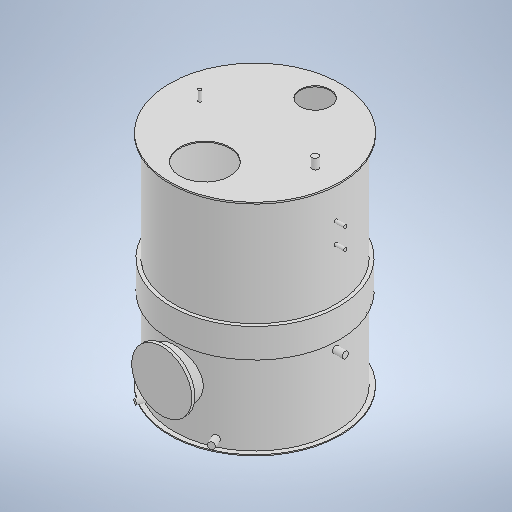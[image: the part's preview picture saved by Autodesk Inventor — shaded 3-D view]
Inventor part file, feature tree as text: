
AUTODESK INVENTOR PART (.ipt)
format: ipt  version: 2025 (Build 290162010, 162A)  size: 396,288 bytes
history: native  units: mm
features: sketch x9, extrude x8, plane x2, revolve x1, shell x1, projected_geometry x1
ambient origin geometry x8: Origin, YZ Plane, XZ Plane, XY Plane, X Axis, Y Axis, Z Axis, Center Point
bodies: Body1 (feature_tree)
feature tree (22):
  revolve  "Revolution1"  [1 undecoded]
  extrude  "Extrusion2"  Depth=1700.0mm
  extrude  "Extrusion8"  Depth=16.0mm
  plane  "Work Plane1"
  plane  "Work Plane2"
  extrude  "Extrusion3"  Depth=1680.0mm
  extrude  "Extrusion4"  Depth=500.0mm
  extrude  "Extrusion5"  Depth=900.0mm TaperAngle=0.0deg
  extrude  "Extrusion6"  Depth=30.0mm TaperAngle=0.0deg
  extrude  "Extrusion7"  Depth=1820.0mm
  extrude  "Extrusion9"  Depth=10.0mm
  shell  "Shell1"  Thickness=65.0mm
  sketch  "Sketch3"  dims[d3=2190.0mm d4=10.0mm]
  sketch  "Sketch4"  dims[d6=1610.0mm d7=1700.0mm]
  sketch  "Sketch5"  dims[d8=16.0mm d9=290.0mm]
  projected_geometry  "Projected Loop2"
  sketch  "Sketch6"  dims[d10=810.0mm d11=1680.0mm]
  sketch  "Sketch7"  dims[d12=90.0deg d13=500.0mm]
  sketch  "Sketch8"  dims[d14=500.0mm d15=900.0mm d16=0.0mm]
  sketch  "Sketch9"  dims[d17=600.0mm d18=30.0mm d19=0.0mm]
  sketch  "Sketch10"  dims[d20=710.0mm d21=1820.0mm]
  sketch  "Sketch11"  dims[d22=1620.0mm d23=32.0mm d24=65.0mm d25=900.0mm d26=0.0mm d27=300.0mm d28=710.0mm d29=1360.0mm d30=65.0mm d31=32.0mm d32=900.0mm d33=0.0mm d34=4.363323mm d35=65.0mm d36=85.0mm d37=900.0mm d38=0.0mm d39=-4.363323mm d40=50.0mm d41=85.0mm d42=900.0mm d43=0.0mm d44=500.0mm d45=300.0mm d46=100.0mm d47=10.0mm d48=0.0mm d49=65.0mm d50=32.0mm d51=250.0mm d52=300.0mm d53=100.0mm d54=0.0mm d55=10.0mm]
note: 1 required parameter value undecoded (feature->parameter linkage not recoverable at this tier; creation-order binding heuristic only, values carry confidence <= 0.55)
